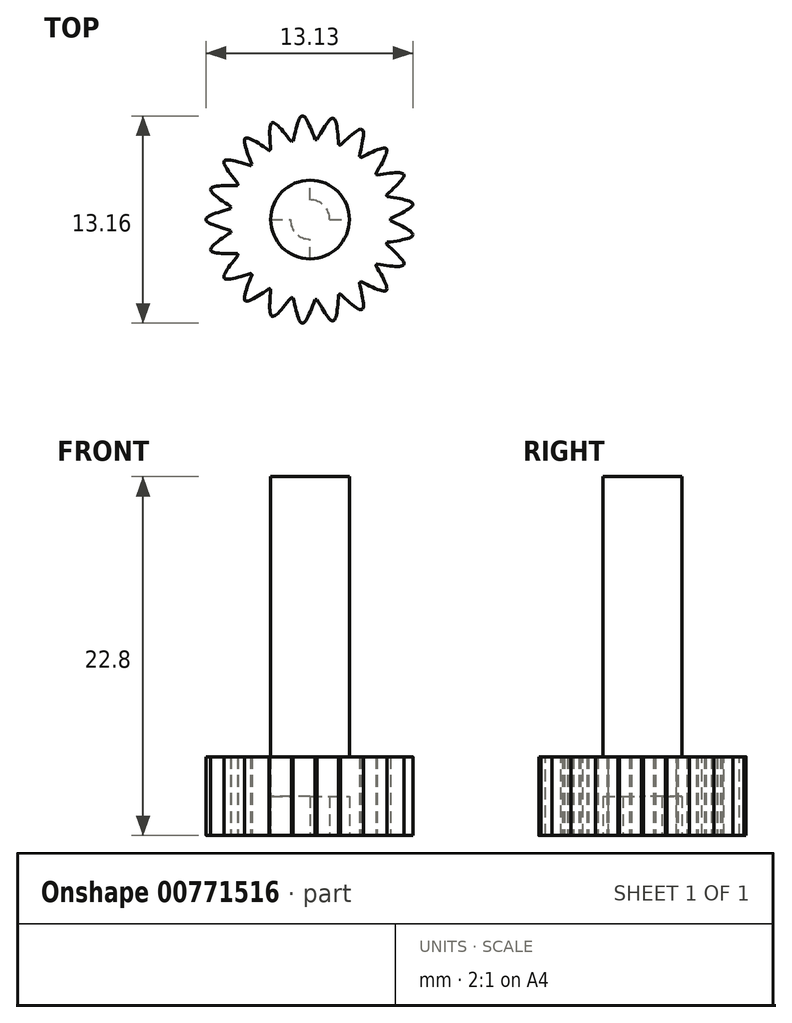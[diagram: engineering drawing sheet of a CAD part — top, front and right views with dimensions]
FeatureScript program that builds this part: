
annotation { "Feature Type Name" : "Feature", "Feature Type Description" : "" }
export const myFeature = defineFeature(function(context is Context, id is Id, definition is map)
    precondition{}
    {
        {
            var Q0;
            Q0=qCreatedBy(makeId("Top.planeOp"),FACE);
            var sketch = newSketch(context, id + "F0", { "sketchPlane" : qUnion([Q0])});
            skLineSegment(sketch, "E0", {"start": v(0, 0) * mm, "end": v(5.1, 0) * mm, "construction": true});
            skLineSegment(sketch, "E1", {"start": v(5.1, 0) * mm, "end": v(-6.6, 0) * mm, "construction": true});
            skCircle(sketch, "E2", {"center": v(0, 0) * mm, "radius": 2.5 * mm});
            skCircle(sketch, "E3", {"center": v(0, 0) * mm, "radius": 5.1 * mm});
            skLineSegment(sketch, "E4", {"start": v(-5.1, 0) * mm, "end": v(-5.1, 0.7) * mm, "construction": true});
            skLineSegment(sketch, "E5", {"start": v(-5.1, 0.7) * mm, "end": v(-5.1, -0.7) * mm, "construction": true});
            skLineSegment(sketch, "E6", {"start": v(-5.1, -0.7) * mm, "end": v(-5.05, -0.7) * mm, "construction": true});
            skLineSegment(sketch, "E7", {"start": v(-5.05, -0.7) * mm, "end": v(-5.05, 0.7) * mm, "construction": true});
            skLineSegment(sketch, "E8", {"start": v(-5.05, 0.7) * mm, "end": v(-5.1, 0.7) * mm, "construction": true});
            skFitSpline(sketch, "E9", {"points": [v(-5.05, -0.7) * mm, v(-6.6, 0) * mm, v(-5.05, 0.7) * mm], "startDerivative": vector(-4.69, 1.4) * mm, "endDerivative": vector(4.69, 1.4) * mm});
            skSolve(sketch);
        }
        {
            var Q0;
            Q0=makeQuery(id+"F0.imprint","IMPRINT",FACE,{"disambiguationData":[TD([[makeQuery(id+"F0.imprint","IMPRINT",EDGE,{"derivedFrom":sQuery(id+"F0.wireOp",EDGE,"E2")}),-1.0]])]});
            var Q1;
            {var subQ0=sQuery(id+"F0.wireOp",EDGE,"E9");Q1=makeQuery(id+"F0.imprint","IMPRINT",FACE,{"disambiguationData":[TD([[makeQuery(id+"F0.imprint","IMPRINT",EDGE,{"derivedFrom":subQ0}),-1.0]])]});}
            extrude(context, id + "F1", {"entities" : qUnion([Q0, Q1]), "depth" : 5 * mm, "offsetDistance" : 25 * mm});
        }
        {
            var Q0;
            Q0=makeQuery(id+"F1.opExtrude","SWEPT_BODY",BODY,{"disambiguationData":[OSD([sQuery(id+"F0.wireOp",EDGE,"E2"),sQuery(id+"F0.wireOp",EDGE,"E3"),sQuery(id+"F0.wireOp",EDGE,"E9")])]});
            var Q1;
            Q1=makeQuery(id+"F1.opExtrude","CAP_EDGE",EDGE,{"disambiguationData":[OSD([sQuery(id+"F0.wireOp",EDGE,"E2")])],"isStart":false});
            circularPattern(context, id + "F2", {"entities" : qUnion([Q0]), "axis" : qUnion([Q1]), "angle" : 360 * degree, "instanceCount" : 21, "equalSpace" : true});
        }
        {
            var Q0;
            Q0=makeQuery(id+"F0.imprint","IMPRINT",FACE,{"disambiguationData":[TD([[makeQuery(id+"F0.imprint","IMPRINT",EDGE,{"derivedFrom":sQuery(id+"F0.wireOp",EDGE,"E2")}),1.0]])]});
            extrude(context, id + "F3", {"entities" : qUnion([Q0]), "operationType" : NewBodyOperationType.ADD, "depth" : 22.8 * mm, "offsetDistance" : 25 * mm});
        }
        {
            var Q0;
            Q0=makeQuery(id+"F0.imprint","IMPRINT",FACE,{"disambiguationData":[TD([[makeQuery(id+"F0.imprint","IMPRINT",EDGE,{"derivedFrom":sQuery(id+"F0.wireOp",EDGE,"E2")}),1.0]])]});
            extrude(context, id + "F4", {"entities" : qUnion([Q0]), "operationType" : NewBodyOperationType.ADD, "oppositeDirection" : true, "depth" : 5 * mm, "offsetDistance" : 25 * mm});
        }
        {
            var Q0;
            Q0=makeQuery(id+"F4.opExtrude","CAP_FACE",FACE,{"disambiguationData":[OSD([sQuery(id+"F0.wireOp",EDGE,"E2")])],"isStart":false});
            var sketch = newSketch(context, id + "F5", { "sketchPlane" : qUnion([Q0])});
            skLineSegment(sketch, "E10", {"start": v(-2.5, 0) * mm, "end": v(2.5, 0) * mm});
            skLineSegment(sketch, "E11", {"start": v(0, 2.5) * mm, "end": v(0, -2.5) * mm});
            skCircle(sketch, "E12", {"center": v(0, 0) * mm, "radius": 1.25 * mm});
            skSolve(sketch);
        }
        {
            var Q0;
            {var subQ0=sQuery(id+"F5.wireOp",EDGE,"E11");var subQ1=sQuery(id+"F5.wireOp",EDGE,"E10");var subQ2=makeQuery(id+"F5.imprint","INTERSECT",VERTEX,{"derivedFrom":[subQ1,subQ0]});Q0=makeQuery(id+"F5.imprint","IMPRINT",FACE,{"disambiguationData":[TD([[makeQuery(id+"F5.imprint","IMPRINT",EDGE,{"disambiguationData":[TD([[subQ2,-1.0]])],"derivedFrom":subQ1}),-1.0]])]});}
            var Q1;
            {var subQ0=sQuery(id+"F5.wireOp",EDGE,"E12");var subQ1=sQuery(id+"F5.wireOp",EDGE,"E10");var subQ2=makeQuery(id+"F5.imprint","INTERSECT",VERTEX,{"disambiguationData":[OD(0.0)],"derivedFrom":[subQ1,subQ0]});Q1=makeQuery(id+"F5.imprint","IMPRINT",FACE,{"disambiguationData":[TD([[makeQuery(id+"F5.imprint","IMPRINT",EDGE,{"disambiguationData":[TD([[subQ2,-1.0]])],"derivedFrom":subQ1}),-1.0]])]});}
            var Q2;
            {var subQ0=sQuery(id+"F5.wireOp",EDGE,"E12");var subQ1=sQuery(id+"F5.wireOp",EDGE,"E10");var subQ2=makeQuery(id+"F5.imprint","INTERSECT",VERTEX,{"disambiguationData":[OD(0.0)],"derivedFrom":[subQ1,subQ0]});Q2=makeQuery(id+"F5.imprint","IMPRINT",FACE,{"disambiguationData":[TD([[makeQuery(id+"F5.imprint","IMPRINT",EDGE,{"disambiguationData":[TD([[subQ2,-1.0]])],"derivedFrom":subQ1}),1.0]])]});}
            var Q3;
            {var subQ0=sQuery(id+"F5.wireOp",EDGE,"E11");var subQ1=sQuery(id+"F5.wireOp",EDGE,"E10");var subQ2=makeQuery(id+"F5.imprint","INTERSECT",VERTEX,{"derivedFrom":[subQ1,subQ0]});Q3=makeQuery(id+"F5.imprint","IMPRINT",FACE,{"disambiguationData":[TD([[makeQuery(id+"F5.imprint","IMPRINT",EDGE,{"disambiguationData":[TD([[subQ2,-1.0]])],"derivedFrom":subQ1}),1.0]])]});}
            var Q4;
            {var subQ0=sQuery(id+"F5.wireOp",EDGE,"E10");var subQ1=makeQuery(id+"F4.opExtrude","CAP_EDGE",EDGE,{"disambiguationData":[OSD([sQuery(id+"F0.wireOp",EDGE,"E2")])],"isStart":false});var subQ2=makeQuery(id+"F5.imprint","INTERSECT",VERTEX,{"disambiguationData":[OD(1.0)],"derivedFrom":[subQ1,subQ0]});Q4=makeQuery(id+"F5.imprint","IMPRINT",FACE,{"disambiguationData":[TD([[makeQuery(id+"F5.imprint","IMPRINT",EDGE,{"disambiguationData":[TD([[subQ2,1.0]])],"derivedFrom":subQ0}),1.0]])]});}
            var Q5;
            {var subQ0=sQuery(id+"F5.wireOp",EDGE,"E10");var subQ1=makeQuery(id+"F4.opExtrude","CAP_EDGE",EDGE,{"disambiguationData":[OSD([sQuery(id+"F0.wireOp",EDGE,"E2")])],"isStart":false});var subQ2=makeQuery(id+"F5.imprint","INTERSECT",VERTEX,{"disambiguationData":[OD(0.0)],"derivedFrom":[subQ1,subQ0]});Q5=makeQuery(id+"F5.imprint","IMPRINT",FACE,{"disambiguationData":[TD([[makeQuery(id+"F5.imprint","IMPRINT",EDGE,{"disambiguationData":[TD([[subQ2,-1.0]])],"derivedFrom":subQ0}),-1.0]])]});}
            extrude(context, id + "F6", {"entities" : qUnion([Q0, Q1, Q2, Q3, Q4, Q5]), "operationType" : NewBodyOperationType.REMOVE, "oppositeDirection" : true, "depth" : 7.5 * mm, "offsetDistance" : 25 * mm});
        }
        {
            var Q0;
            {var subQ0=sQuery(id+"F0.wireOp",EDGE,"E2");var subQ1=sQuery(id+"F5.wireOp",EDGE,"E10");var subQ2=makeQuery(id+"F4.opExtrude","CAP_EDGE",EDGE,{"disambiguationData":[OSD([subQ0])],"isStart":false});Q0=makeQuery(id+"F6.boolean.opBoolean","SPLIT",FACE,{"disambiguationData":[TD([makeQuery(id+"F6.opExtrude","SWEPT_FACE",FACE,{"disambiguationData":[OSD([subQ1]),TDD([makeQuery(id+"F5.imprint","IMPRINT",EDGE,{"disambiguationData":[TD([[makeQuery(id+"F5.imprint","INTERSECT",VERTEX,{"disambiguationData":[OD(1.0)],"derivedFrom":[subQ2,subQ1]}),1.0]])],"derivedFrom":subQ1})])]})])],"derivedFrom":makeQuery(id+"F4.opExtrude","CAP_FACE",FACE,{"disambiguationData":[OSD([subQ0])],"isStart":false})});}
            var Q1;
            {var subQ0=sQuery(id+"F0.wireOp",EDGE,"E2");var subQ2=sQuery(id+"F5.wireOp",EDGE,"E10");var subQ6=makeQuery(id+"F4.opExtrude","CAP_EDGE",EDGE,{"disambiguationData":[OSD([subQ0])],"isStart":false});Q1=makeQuery(id+"F6.boolean.opBoolean","SPLIT",FACE,{"disambiguationData":[TD([makeQuery(id+"F6.opExtrude","SWEPT_FACE",FACE,{"disambiguationData":[OSD([subQ2]),TDD([makeQuery(id+"F5.imprint","IMPRINT",EDGE,{"disambiguationData":[TD([[makeQuery(id+"F5.imprint","INTERSECT",VERTEX,{"disambiguationData":[OD(0.0)],"derivedFrom":[subQ6,subQ2]}),-1.0]])],"derivedFrom":subQ2})])]})])],"derivedFrom":makeQuery(id+"F4.opExtrude","CAP_FACE",FACE,{"disambiguationData":[OSD([subQ0])],"isStart":false})});}
            extrude(context, id + "F7", {"entities" : qUnion([Q0, Q1]), "operationType" : NewBodyOperationType.REMOVE, "oppositeDirection" : true, "depth" : 5 * mm, "offsetDistance" : 25 * mm});
        }
    });
